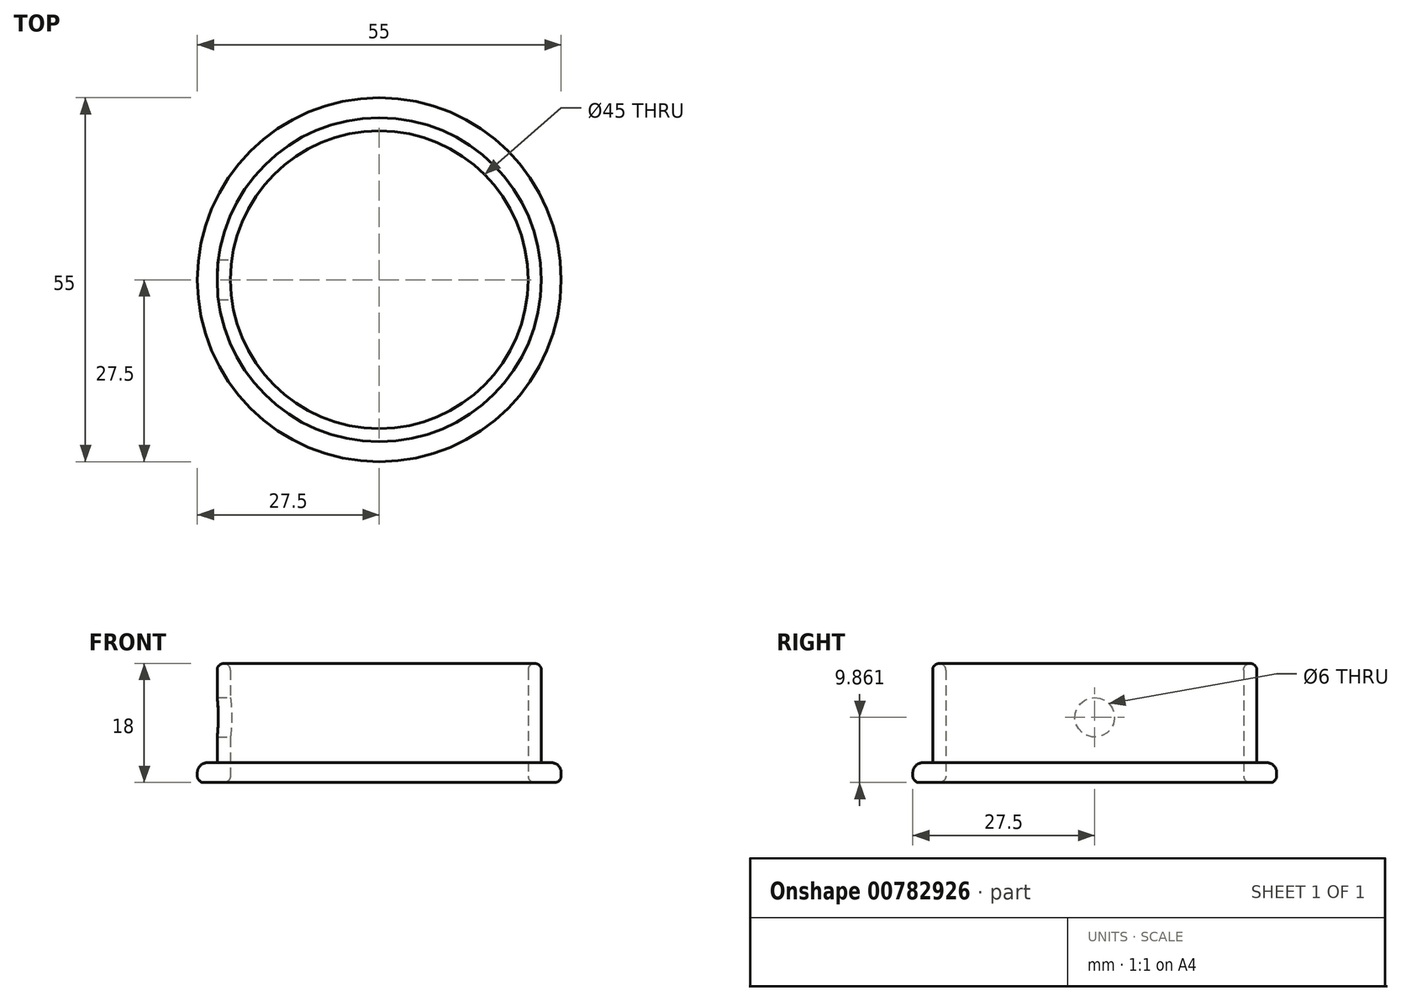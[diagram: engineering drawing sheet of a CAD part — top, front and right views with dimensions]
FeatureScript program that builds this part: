
annotation { "Feature Type Name" : "Feature", "Feature Type Description" : "" }
export const myFeature = defineFeature(function(context is Context, id is Id, definition is map)
    precondition{}
    {
        {
            var Q0;
            Q0=qCreatedBy(makeId("Top.planeOp"),FACE);
            var sketch = newSketch(context, id + "F0", { "sketchPlane" : qUnion([Q0])});
            skCircle(sketch, "E0", {"center": v(0, 0) * mm, "radius": 27.5 * mm});
            skCircle(sketch, "E1", {"center": v(0, 0) * mm, "radius": 24.5 * mm});
            skCircle(sketch, "E2", {"center": v(0, 0) * mm, "radius": 22.5 * mm});
            skSolve(sketch);
        }
        {
            var Q0;
            Q0=makeQuery(id+"F0.imprint","IMPRINT",FACE,{"disambiguationData":[TD([[makeQuery(id+"F0.imprint","IMPRINT",EDGE,{"derivedFrom":sQuery(id+"F0.wireOp",EDGE,"E0")}),1.0]])]});
            extrude(context, id + "F1", {"entities" : qUnion([Q0]), "depth" : 3 * mm, "offsetDistance" : 25 * mm});
        }
        {
            var Q0;
            Q0=makeQuery(id+"F0.imprint","IMPRINT",FACE,{"disambiguationData":[TD([[makeQuery(id+"F0.imprint","IMPRINT",EDGE,{"derivedFrom":sQuery(id+"F0.wireOp",EDGE,"E1")}),1.0]])]});
            extrude(context, id + "F2", {"entities" : qUnion([Q0]), "operationType" : NewBodyOperationType.ADD, "depth" : 18 * mm, "offsetDistance" : 25 * mm});
        }
        {
            var Q0;
            Q0=makeQuery(id+"F1.opExtrude","CAP_EDGE",EDGE,{"disambiguationData":[OSD([sQuery(id+"F0.wireOp",EDGE,"E0")])],"isStart":true});
            var Q1;
            Q1=makeQuery(id+"F2.opExtrude","CAP_EDGE",EDGE,{"disambiguationData":[OSD([sQuery(id+"F0.wireOp",EDGE,"E2")])],"isStart":true});
            fillet(context, id + "F3", {"entities" : qUnion([Q0, Q1]), "radius" : 1 * mm, "tangentPropagation" : true, "allowEdgeOverflow" : false});
        }
        {
            var Q0;
            Q0=makeQuery(id+"F1.opExtrude","CAP_EDGE",EDGE,{"disambiguationData":[OSD([sQuery(id+"F0.wireOp",EDGE,"E0")])],"isStart":false});
            fillet(context, id + "F4", {"entities" : qUnion([Q0]), "radius" : 1.5 * mm, "tangentPropagation" : true, "allowEdgeOverflow" : false});
        }
        {
            var Q0;
            Q0=makeQuery(id+"F2.opExtrude","CAP_EDGE",EDGE,{"disambiguationData":[OSD([sQuery(id+"F0.wireOp",EDGE,"E2")])],"isStart":false});
            var Q1;
            Q1=makeQuery(id+"F2.opExtrude","CAP_EDGE",EDGE,{"disambiguationData":[OSD([sQuery(id+"F0.wireOp",EDGE,"E1")])],"isStart":false});
            fillet(context, id + "F5", {"entities" : qUnion([Q0, Q1]), "radius" : 1 * mm, "tangentPropagation" : true, "allowEdgeOverflow" : false});
        }
        {
            var Q0;
            Q0=qCreatedBy(makeId("Right.planeOp"),FACE);
            var sketch = newSketch(context, id + "F6", { "sketchPlane" : qUnion([Q0])});
            skLineSegment(sketch, "E3", {"start": v(0, 9.86) * mm, "end": v(0, 23.88) * mm});
            skSolve(sketch);
        }
        {
            var Q0;
            Q0=sQuery(id+"F6.wireOp",VERTEX,"E3.start");
            var Q1;
            Q1=makeQuery(id+"F1.opExtrude","SWEPT_BODY",BODY,{"disambiguationData":[OSD([sQuery(id+"F0.wireOp",EDGE,"E0"),sQuery(id+"F0.wireOp",EDGE,"E1")])]});
            hole(context, id + "F7", {"style" : HoleStyle.SIMPLE, "endStyle" : HoleEndStyle.BLIND, "holeDiameter" : 6 * mm, "majorDiameter" : 5 * mm, "holeDepth" : 25 * mm, "isTappedThrough" : true, "tappedDepth" : 12 * mm, "tapClearance" : 3, "locations" : qUnion([Q0]), "scope" : qUnion([Q1])});
        }
    });
